# Revit family: Gira_134928
name_source: partatom
category: Electrical Fixtures
revit_build: Autodesk Revit 2017 (Build: 20160225_1515(x64)
units: mm (PartAtom-declared; Revit-internal decimal feet)

## family parameters
Cut with Voids When Loaded = No
Host = Face
Maintain Annotation Orientation = Yes
Part Type = Normal
Room Calculation Point = No
Round Connector Dimension = Use Diameter
Shared = No

## types (1)
- En.prof. light el. 3x empty u. 769 mm Gira energy profile anthra.
    Available = No
    BIM (1) = https://media.stage.bim.site
    Category = Light/energy pole
    Data sheet (1) = https://katalog.gira.de
    Default Elevation = 1219 mm
    Depth = 0,075
    Description = 769 mm light 3x empty u. E-pro AN,Gira energy profile,Light element, 3 empty units, height 769 mm ,anthracite,The Gira energy profile and light profiles for outdoor use, with and without light elements. The profiles consist of powder-coated aluminium. For profiles of up to 1400 mm, the feet elements also consist of powder-coated aluminium. For profiles of more than 1400 mm, the feet elements consist of powder-coated steel. Also in the colour anthracite in accordance with the GSB standard. The surface is is resistant to weather, UV rays, dirt and scratches.,,Notes :,- For profile heights up to 1400 mm, an optional ground anchor can be used to facilitate mounting on a stone or concrete base.,- For profile heights of more than 1400 mm, mounting on stone or concrete is only possible using 3 heavy-duty wall anchor.,- Recommendation: Mount an RCCB prior to the device.
    GTIN = 4010337349280
    HAN = 134928
    Height = 0,769
    HeinzeBIM = https://bimportal.heinze.de
    Manufacturer = Gira
    Manufacturer URL = https://www.gira.de
    Name = En.prof. light el. 3x empty u. 769 mm Gira energy profile anthra.
    Number of socket outlets = 0
    Switching function = None
    URL = http://katalog.gira.de
    Width = 0,142

## geometry (parser evidence)
native form markers: Blend x2, Sweep x3
no freeform markers — native parametric forms only
